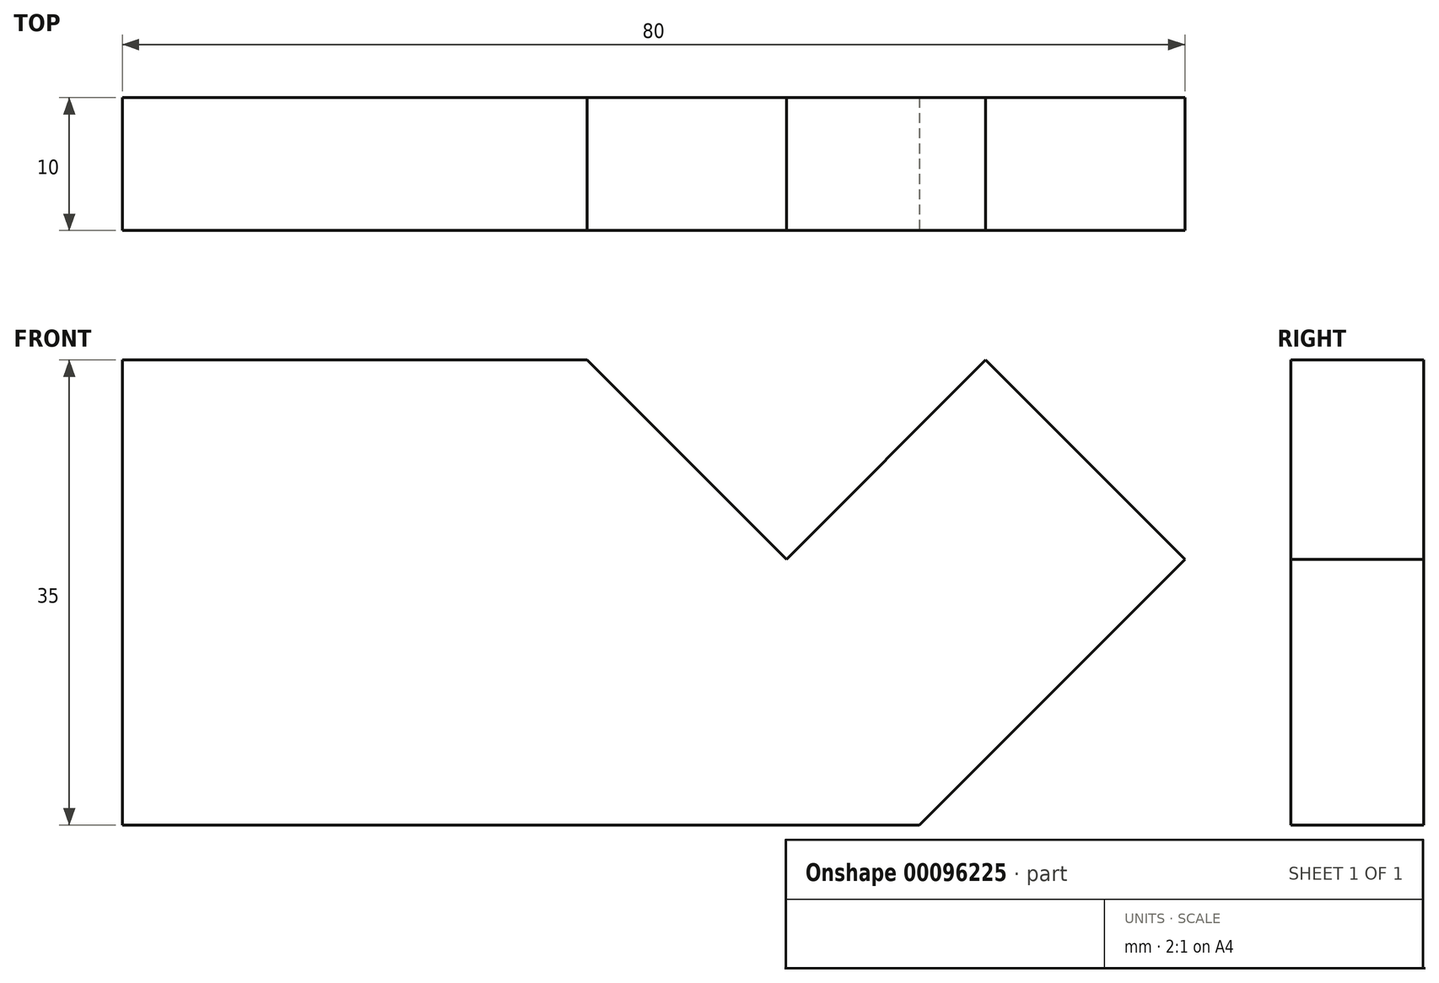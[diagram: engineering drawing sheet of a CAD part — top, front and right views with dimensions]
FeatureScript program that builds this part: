
annotation { "Feature Type Name" : "Feature", "Feature Type Description" : "" }
export const myFeature = defineFeature(function(context is Context, id is Id, definition is map)
    precondition{}
    {
        {
            var Q0;
            Q0=qCreatedBy(makeId("Front.planeOp"),FACE);
            var sketch = newSketch(context, id + "F0", { "sketchPlane" : qUnion([Q0])});
            skLineSegment(sketch, "E0", {"start": v(0, 0) * mm, "end": v(60, 0) * mm});
            skLineSegment(sketch, "E1", {"start": v(60, 0) * mm, "end": v(80, 20) * mm});
            skLineSegment(sketch, "E2", {"start": v(80, 20) * mm, "end": v(65, 35) * mm});
            skLineSegment(sketch, "E3", {"start": v(65, 35) * mm, "end": v(50, 20) * mm});
            skLineSegment(sketch, "E4", {"start": v(50, 20) * mm, "end": v(35, 35) * mm});
            skLineSegment(sketch, "E5", {"start": v(35, 35) * mm, "end": v(0, 35) * mm});
            skLineSegment(sketch, "E6", {"start": v(0, 35) * mm, "end": v(0, 0) * mm});
            skLineSegment(sketch, "E7", {"start": v(35, 35) * mm, "end": v(65, 35) * mm, "construction": true});
            skSolve(sketch);
        }
        {
            var Q0;
            Q0=makeQuery(id+"F0.imprint","IMPRINT",FACE,{"disambiguationData":[TD([[makeQuery(id+"F0.imprint","IMPRINT",EDGE,{"derivedFrom":sQuery(id+"F0.wireOp",EDGE,"E0")}),1.0]])]});
            extrude(context, id + "F1", {"entities" : qUnion([Q0]), "endBound" : BoundingType.SYMMETRIC, "oppositeDirection" : true, "depth" : 10 * mm});
        }
    });
